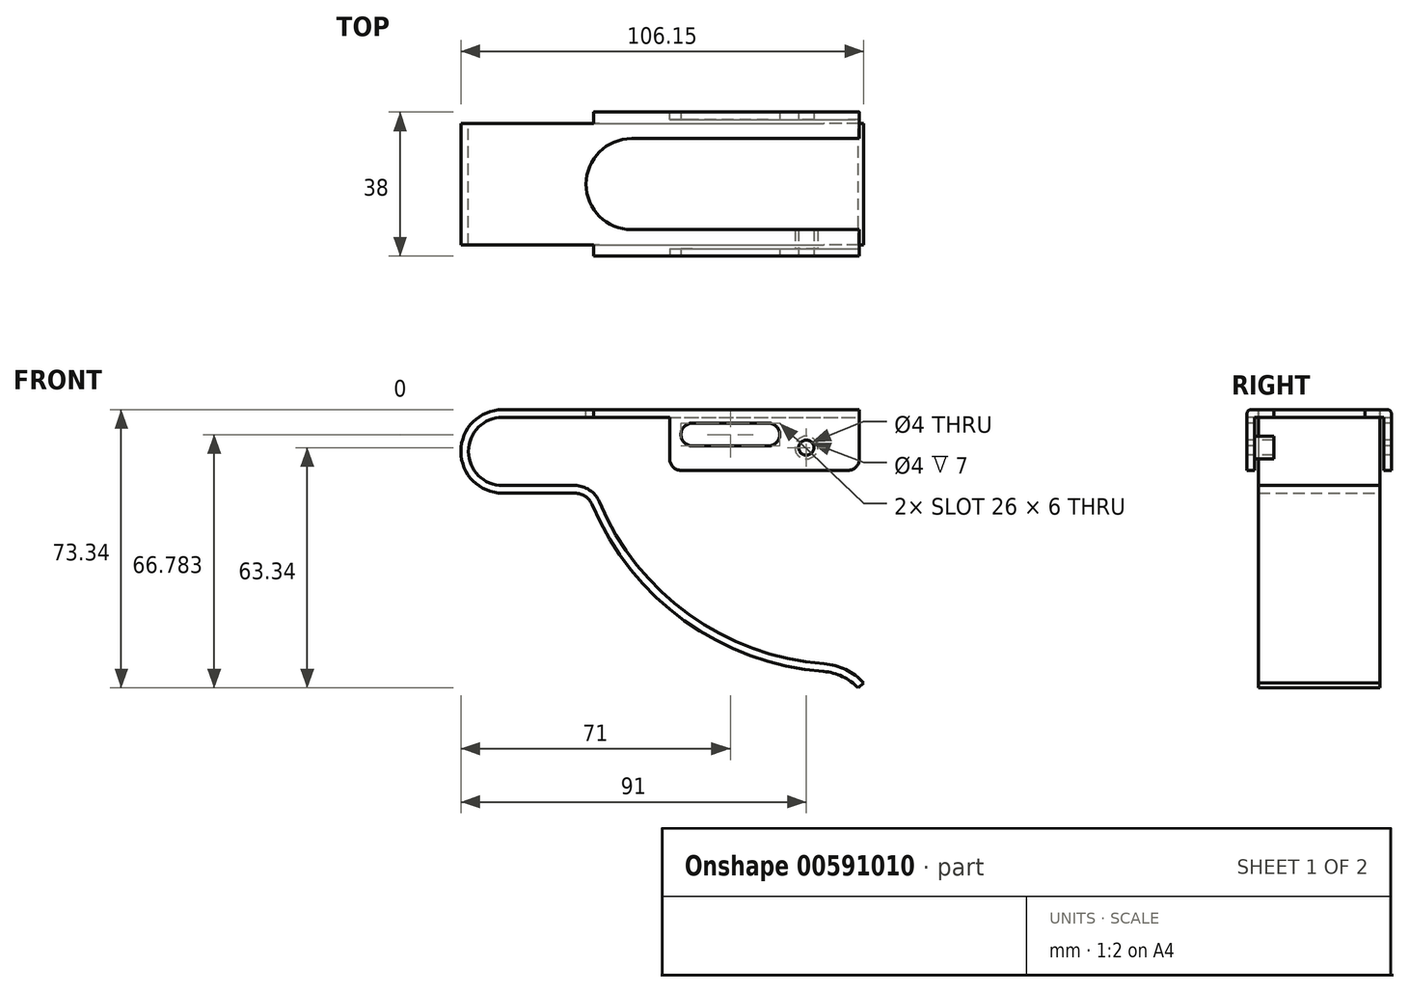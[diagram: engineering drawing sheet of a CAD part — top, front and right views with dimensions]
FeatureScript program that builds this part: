
annotation { "Feature Type Name" : "Feature", "Feature Type Description" : "" }
export const myFeature = defineFeature(function(context is Context, id is Id, definition is map)
    precondition{}
    {
        {
            var Q0;
            Q0=qCreatedBy(makeId("Front.planeOp"),FACE);
            var sketch = newSketch(context, id + "F0", { "sketchPlane" : qUnion([Q0])});
            skArc(sketch, "E0", {"start": v(0, 11) * mm, "mid": v(-11, 0) * mm, "end": v(0, -11) * mm});
            skLineSegment(sketch, "E1", {"start": v(0, 11) * mm, "end": v(94, 11) * mm});
            skLineSegment(sketch, "E2", {"start": v(0, -11) * mm, "end": v(19, -11) * mm});
            skArc(sketch, "E3", {"start": v(23.61, -14.06) * mm, "mid": v(47.9, -44.6) * mm, "end": v(84.55, -58) * mm});
            skPoint(sketch, "E4.visualSharp", {"position": v(22.4, -11) * mm});
            skArc(sketch, "E4.filletArc", {"start": v(23.61, -14.06) * mm, "mid": v(21.77, -11.84) * mm, "end": v(19, -11) * mm});
            skArc(sketch, "E5", {"start": v(93.67, -62.34) * mm, "mid": v(89.52, -59.32) * mm, "end": v(84.55, -58) * mm});
            skLineSegment(sketch, "E6.0", {"start": v(0, 9) * mm, "end": v(94, 9) * mm});
            skArc(sketch, "E6.1", {"start": v(0, 9) * mm, "mid": v(-9, 0) * mm, "end": v(0, -9) * mm});
            skArc(sketch, "E6.2", {"start": v(95.15, -61) * mm, "mid": v(90.4, -57.52) * mm, "end": v(84.7, -56) * mm});
            skArc(sketch, "E6.3", {"start": v(25.45, -13.3) * mm, "mid": v(49.07, -42.99) * mm, "end": v(84.7, -56) * mm});
            skArc(sketch, "E6.4", {"start": v(25.45, -13.3) * mm, "mid": v(22.88, -10.17) * mm, "end": v(19, -9) * mm});
            skLineSegment(sketch, "E6.5", {"start": v(0, -9) * mm, "end": v(19, -9) * mm});
            skLineSegment(sketch, "E7", {"start": v(94, 9) * mm, "end": v(94, 11) * mm});
            skLineSegment(sketch, "E8", {"start": v(93.67, -62.34) * mm, "end": v(95.15, -61) * mm});
            skLineSegment(sketch, "E9", {"start": v(95.15, -61) * mm, "end": v(99.01, -61) * mm, "construction": true});
            skSolve(sketch);
        }
        {
            var Q0;
            Q0 = qSketchRegion(id + "F0", true);
            extrude(context, id + "F1", {"entities" : qUnion([Q0]), "depth" : 16 * mm, "offsetDistance" : 25 * mm});
        }
        {
            var Q0;
            Q0=makeQuery(id+"F1.opExtrude","SWEPT_FACE",FACE,{"disambiguationData":[OSD([sQuery(id+"F0.wireOp",EDGE,"E1")])]});
            var sketch = newSketch(context, id + "F2", { "sketchPlane" : qUnion([Q0])});
            skLineSegment(sketch, "E10.bottom", {"start": v(24, -16) * mm, "end": v(94, -16) * mm});
            skLineSegment(sketch, "E10.top", {"start": v(24, -19) * mm, "end": v(94, -19) * mm});
            skLineSegment(sketch, "E10.left", {"start": v(24, -16) * mm, "end": v(24, -19) * mm});
            skLineSegment(sketch, "E10.right", {"start": v(94, -16) * mm, "end": v(94, -19) * mm});
            skSolve(sketch);
        }
        {
            var Q0;
            Q0 = qSketchRegion(id + "F2", true);
            extrude(context, id + "F3", {"entities" : qUnion([Q0]), "operationType" : NewBodyOperationType.ADD, "oppositeDirection" : true, "depth" : 2 * mm, "offsetDistance" : 25 * mm});
        }
        {
            var Q0;
            Q0=makeQuery(id+"F3.opExtrude","SWEPT_FACE",FACE,{"disambiguationData":[OSD([sQuery(id+"F2.wireOp",EDGE,"E10.top")])]});
            var sketch = newSketch(context, id + "F4", { "sketchPlane" : qUnion([Q0])});
            skLineSegment(sketch, "E11.bottom", {"start": v(24, 9) * mm, "end": v(94, 9) * mm});
            skLineSegment(sketch, "E11.top", {"start": v(44, -5) * mm, "end": v(94, -5) * mm});
            skLineSegment(sketch, "E11.left", {"start": v(44, 9) * mm, "end": v(44, -5) * mm});
            skLineSegment(sketch, "E11.right", {"start": v(94, 9) * mm, "end": v(94, -5) * mm});
            skSolve(sketch);
        }
        {
            var Q0;
            Q0 = qSketchRegion(id + "F4", true);
            extrude(context, id + "F5", {"entities" : qUnion([Q0]), "operationType" : NewBodyOperationType.ADD, "oppositeDirection" : true, "depth" : 2 * mm, "offsetDistance" : 25 * mm});
        }
        {
            var Q0;
            Q0=makeQuery(id+"F3.opExtrude","CAP_EDGE",EDGE,{"disambiguationData":[OSD([sQuery(id+"F2.wireOp",EDGE,"E10.top")])],"isStart":true});
            fillet(context, id + "F6", {"entities" : qUnion([Q0]), "radius" : 1 * mm, "allowEdgeOverflow" : false});
        }
        {
            var Q0;
            Q0=makeQuery(id+"F1.opExtrude","SWEPT_BODY",BODY,{"disambiguationData":[OSD([sQuery(id+"F0.wireOp",EDGE,"E0"),sQuery(id+"F0.wireOp",EDGE,"E1"),sQuery(id+"F0.wireOp",EDGE,"E2"),sQuery(id+"F0.wireOp",EDGE,"E3"),sQuery(id+"F0.wireOp",EDGE,"E4.filletArc"),sQuery(id+"F0.wireOp",EDGE,"E5"),sQuery(id+"F0.wireOp",EDGE,"E6.0"),sQuery(id+"F0.wireOp",EDGE,"E6.1"),sQuery(id+"F0.wireOp",EDGE,"E6.2"),sQuery(id+"F0.wireOp",EDGE,"E6.3"),sQuery(id+"F0.wireOp",EDGE,"E6.4"),sQuery(id+"F0.wireOp",EDGE,"E6.5"),sQuery(id+"F0.wireOp",EDGE,"E7"),sQuery(id+"F0.wireOp",EDGE,"E8")])]});
            var Q1;
            Q1=qCreatedBy(makeId("Front.planeOp"),FACE);
            mirror(context, id + "F7", {"operationType" : NewBodyOperationType.ADD, "entities" : qUnion([Q0]), "mirrorPlane" : qUnion([Q1])});
        }
        {
            var Q0;
            {var subQ0=makeQuery(id+"F3.boolean.opBoolean","MERGE",FACE,{"derivedFrom":[makeQuery(id+"F1.opExtrude","SWEPT_FACE",FACE,{"disambiguationData":[OSD([sQuery(id+"F0.wireOp",EDGE,"E1")])]}),makeQuery(id+"F3.opExtrude","CAP_FACE",FACE,{"disambiguationData":[OSD([sQuery(id+"F2.wireOp",EDGE,"E10.bottom"),sQuery(id+"F2.wireOp",EDGE,"E10.top"),sQuery(id+"F2.wireOp",EDGE,"E10.left"),sQuery(id+"F2.wireOp",EDGE,"E10.right")])],"isStart":true})]});Q0=makeQuery(id+"F7.boolean.opBoolean","MERGE",FACE,{"derivedFrom":[subQ0,makeQuery(id+"F7.opPattern","COPY",FACE,{"derivedFrom":subQ0,"instanceName":"1"})]});}
            var sketch = newSketch(context, id + "F8", { "sketchPlane" : qUnion([Q0])});
            skArc(sketch, "E12", {"start": v(34, 12) * mm, "mid": v(22, 0) * mm, "end": v(34, -12) * mm});
            skLineSegment(sketch, "E13", {"start": v(34, 12) * mm, "end": v(94, 12) * mm});
            skLineSegment(sketch, "E14", {"start": v(34, -12) * mm, "end": v(94, -12) * mm});
            skLineSegment(sketch, "E15", {"start": v(94, 12) * mm, "end": v(94, -12) * mm});
            skSolve(sketch);
        }
        {
            var Q0;
            Q0 = qSketchRegion(id + "F8", true);
            extrude(context, id + "F9", {"entities" : qUnion([Q0]), "operationType" : NewBodyOperationType.REMOVE, "oppositeDirection" : true, "depth" : 2 * mm, "offsetDistance" : 25 * mm});
        }
        {
            var Q0;
            Q0=makeQuery(id+"F5.boolean.opBoolean","MERGE",FACE,{"derivedFrom":[makeQuery(id+"F3.opExtrude","SWEPT_FACE",FACE,{"disambiguationData":[OSD([sQuery(id+"F2.wireOp",EDGE,"E10.top")])]}),makeQuery(id+"F5.opExtrude","CAP_FACE",FACE,{"disambiguationData":[OSD([sQuery(id+"F4.wireOp",EDGE,"E11.bottom"),sQuery(id+"F4.wireOp",EDGE,"E11.top"),sQuery(id+"F4.wireOp",EDGE,"E11.left"),sQuery(id+"F4.wireOp",EDGE,"E11.right")])],"isStart":true})]});
            var sketch = newSketch(context, id + "F10", { "sketchPlane" : qUnion([Q0])});
            skLineSegment(sketch, "E16", {"start": v(50, 4.44) * mm, "end": v(70, 4.44) * mm});
            skArc(sketch, "E17.0.startCap", {"start": v(50, 1.44) * mm, "mid": v(47, 4.44) * mm, "end": v(50, 7.44) * mm});
            skArc(sketch, "E17.0.endCap", {"start": v(70, 7.44) * mm, "mid": v(73, 4.44) * mm, "end": v(70, 1.44) * mm});
            skLineSegment(sketch, "E17.0.left", {"start": v(50, 7.44) * mm, "end": v(70, 7.44) * mm});
            skLineSegment(sketch, "E17.0.right", {"start": v(50, 1.44) * mm, "end": v(70, 1.44) * mm});
            skSolve(sketch);
        }
        {
            var Q0;
            Q0 = qSketchRegion(id + "F10", true);
            extrude(context, id + "F11", {"entities" : qUnion([Q0]), "operationType" : NewBodyOperationType.REMOVE, "endBound" : BoundingType.THROUGH_ALL, "oppositeDirection" : true, "depth" : 25 * mm, "offsetDistance" : 25 * mm});
        }
        {
            var Q0;
            Q0=makeQuery(id+"F5.boolean.opBoolean","MERGE",FACE,{"derivedFrom":[makeQuery(id+"F3.opExtrude","SWEPT_FACE",FACE,{"disambiguationData":[OSD([sQuery(id+"F2.wireOp",EDGE,"E10.top")])]}),makeQuery(id+"F5.opExtrude","CAP_FACE",FACE,{"disambiguationData":[OSD([sQuery(id+"F4.wireOp",EDGE,"E11.bottom"),sQuery(id+"F4.wireOp",EDGE,"E11.top"),sQuery(id+"F4.wireOp",EDGE,"E11.left"),sQuery(id+"F4.wireOp",EDGE,"E11.right")])],"isStart":true})]});
            var sketch = newSketch(context, id + "F12", { "sketchPlane" : qUnion([Q0])});
            skPoint(sketch, "E18", {"position": v(80, 1) * mm});
            skSolve(sketch);
        }
        {
            var Q0;
            Q0=sQuery(id+"F12.wireOp",VERTEX,"E18");
            var Q1;
            Q1=makeQuery(id+"F1.opExtrude","SWEPT_BODY",BODY,{"disambiguationData":[OSD([sQuery(id+"F0.wireOp",EDGE,"E0"),sQuery(id+"F0.wireOp",EDGE,"E1"),sQuery(id+"F0.wireOp",EDGE,"E2"),sQuery(id+"F0.wireOp",EDGE,"E3"),sQuery(id+"F0.wireOp",EDGE,"E4.filletArc"),sQuery(id+"F0.wireOp",EDGE,"E5"),sQuery(id+"F0.wireOp",EDGE,"E6.0"),sQuery(id+"F0.wireOp",EDGE,"E6.1"),sQuery(id+"F0.wireOp",EDGE,"E6.2"),sQuery(id+"F0.wireOp",EDGE,"E6.3"),sQuery(id+"F0.wireOp",EDGE,"E6.4"),sQuery(id+"F0.wireOp",EDGE,"E6.5"),sQuery(id+"F0.wireOp",EDGE,"E7"),sQuery(id+"F0.wireOp",EDGE,"E8")])]});
            hole(context, id + "F13", {"style" : HoleStyle.SIMPLE, "endStyle" : HoleEndStyle.THROUGH, "holeDiameter" : 4 * mm, "majorDiameter" : 5 * mm, "isTappedThrough" : true, "tappedDepth" : 12 * mm, "tapClearance" : 3, "locations" : qUnion([Q0]), "scope" : qUnion([Q1])});
        }
        {
            var Q0;
            Q0=makeQuery(id+"F5.opExtrude","CAP_FACE",FACE,{"disambiguationData":[OSD([sQuery(id+"F4.wireOp",EDGE,"E11.bottom"),sQuery(id+"F4.wireOp",EDGE,"E11.top"),sQuery(id+"F4.wireOp",EDGE,"E11.left"),sQuery(id+"F4.wireOp",EDGE,"E11.right")])],"isStart":false});
            var sketch = newSketch(context, id + "F14", { "sketchPlane" : qUnion([Q0])});
            skCircle(sketch, "E19.1", {"center": v(-80, 1) * mm, "radius": 2 * mm});
            skCircle(sketch, "E20.0", {"center": v(-80, 1) * mm, "radius": 3 * mm});
            skSolve(sketch);
        }
        {
            var Q0;
            Q0 = qSketchRegion(id + "F14", true);
            extrude(context, id + "F15", {"entities" : qUnion([Q0]), "operationType" : NewBodyOperationType.ADD, "depth" : 5 * mm, "offsetDistance" : 25 * mm});
        }
        {
            var Q0;
            Q0=makeQuery(id+"F7.opPattern","COPY",EDGE,{"derivedFrom":makeQuery(id+"F5.opExtrude","SWEPT_EDGE",EDGE,{"disambiguationData":[OSD([sQuery(id+"F4.wireOp",EDGE,"E11.top"),sQuery(id+"F4.wireOp",EDGE,"E11.right")])]}),"instanceName":"1"});
            var Q1;
            Q1=makeQuery(id+"F7.opPattern","COPY",EDGE,{"derivedFrom":makeQuery(id+"F5.opExtrude","SWEPT_EDGE",EDGE,{"disambiguationData":[OSD([sQuery(id+"F4.wireOp",EDGE,"E11.top"),sQuery(id+"F4.wireOp",EDGE,"E11.left")])]}),"instanceName":"1"});
            var Q2;
            Q2=makeQuery(id+"F5.opExtrude","SWEPT_EDGE",EDGE,{"disambiguationData":[OSD([sQuery(id+"F4.wireOp",EDGE,"E11.top"),sQuery(id+"F4.wireOp",EDGE,"E11.right")])]});
            var Q3;
            Q3=makeQuery(id+"F5.opExtrude","SWEPT_EDGE",EDGE,{"disambiguationData":[OSD([sQuery(id+"F4.wireOp",EDGE,"E11.top"),sQuery(id+"F4.wireOp",EDGE,"E11.left")])]});
            fillet(context, id + "F16", {"entities" : qUnion([Q0, Q1, Q2, Q3]), "radius" : 3 * mm, "tangentPropagation" : true, "allowEdgeOverflow" : false});
        }
    });
